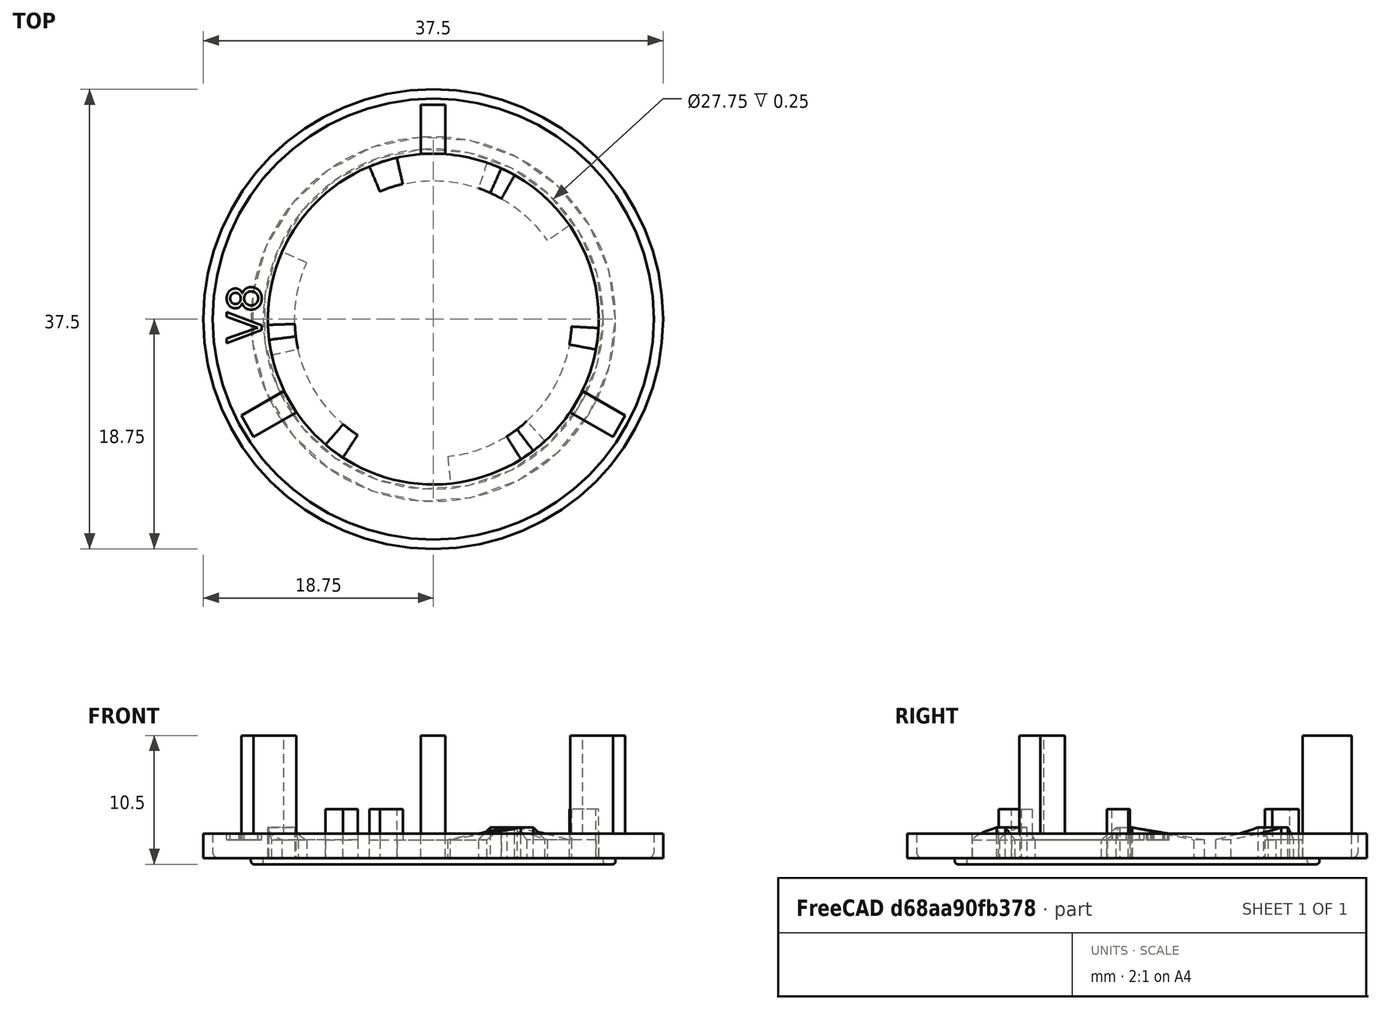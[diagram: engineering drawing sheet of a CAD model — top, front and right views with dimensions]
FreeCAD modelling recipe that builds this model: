
FCSTD DOCUMENT  (FreeCAD 0.19R21857 (Git))
Label: BayonetBaseFemaleV8
License: All rights reserved
LicenseURL: http://en.wikipedia.org/wiki/All_rights_reserved
objects: Sketcher::SketchObject×40, Part::Sweep×16, Part::MultiFuse×10, Part::Fillet×4, Part::Cylinder×3, Part::Mirroring×3, Part::Cut×2, PartDesign::Body×1, Part::Box×1, Image::ImagePlane×1, Part::FeaturePython×1, Part::Part2DObjectPython×1, Part::Extrusion×1, Mesh::Feature×1
note: 82 computed .brp shape members not serialized (recipe doc carries the construction recipe); baked Part::Feature solids carry a one-line shape summary decoded from their .brp

FEATURE [Part::Cylinder] Cylinder
  Angle = 360
  AttacherType = Attacher::AttachEngine3D
  Height = 2
  Radius = 18.75
FEATURE [Sketcher::SketchObject] Sketch  label="RampStart"
  Placement = pos=(0,0,0) rot=(1,0,0;1.5708rad)
  sketch-geometry (4):
    g0: LineSegment StartX=-13.5 StartY=0 StartZ=0 EndX=-13.5 EndY=1.5 EndZ=0
    g1: LineSegment StartX=-13.5 StartY=1.5 StartZ=0 EndX=-11.3 EndY=1.5 EndZ=0
    g2: LineSegment StartX=-11.3 StartY=1.5 StartZ=0 EndX=-11.3 EndY=0 EndZ=0
    g3: LineSegment StartX=-11.3 StartY=0 StartZ=0 EndX=-13.5 EndY=0 EndZ=0
  constraints (12):
    c: Coincident(g0,g1)
    c: Coincident(g1,g2)
    c: Coincident(g2,g3)
    c: Coincident(g3,g0)
    c: Parallel(g0,g2)
    c: Parallel(g1,g3)
    c: Horizontal(g3)
    c: Vertical(g2)
    c: DistanceY(g-1,g2) = 0
    c: DistanceX(g2,g-1) = 11.3
    c: DistanceX(g0,g-1) = 13.5
    c: DistanceY(g0,g0) = 1.5
FEATURE [Sketcher::SketchObject] Sketch001  label="InnerCircumference"
  Placement = pos=(0,0,0) rot=(1,0,0;3.14159rad)
  sketch-geometry (1):
    g0: Circle CenterX=0 CenterY=0 CenterZ=0 NormalX=0 NormalY=0 NormalZ=1 AngleXU=0 Radius=11
  constraints (1):
    c: Radius(g0) = 11
FEATURE [Sketcher::SketchObject] Sketch002  label="RampEnd"
  Placement = pos=(0,0,0) rot=(0.950615,-0.219467,-0.219467;1.62142rad)
  sketch-geometry (4):
    g0: LineSegment StartX=-13.5 StartY=0 StartZ=0 EndX=-13.5 EndY=2.5 EndZ=0
    g1: LineSegment StartX=-13.5 StartY=2.5 StartZ=0 EndX=-11.3 EndY=2.5 EndZ=0
    g2: LineSegment StartX=-11.3 StartY=2.5 StartZ=0 EndX=-11.3 EndY=0 EndZ=0
    g3: LineSegment StartX=-11.3 StartY=0 StartZ=0 EndX=-13.5 EndY=0 EndZ=0
  constraints (12):
    c: Coincident(g0,g1)
    c: Coincident(g1,g2)
    c: Coincident(g2,g3)
    c: Coincident(g3,g0)
    c: Parallel(g0,g2)
    c: Parallel(g1,g3)
    c: Horizontal(g3)
    c: Vertical(g2)
    c: DistanceY(g-1,g2) = 0
    c: DistanceX(g2,g-1) = 11.3
    c: DistanceX(g0,g-1) = 13.5
    c: DistanceY(g0,g0) = 2.5
FEATURE [Sketcher::SketchObject] Sketch003  label="RampFlat"
  Placement = pos=(0,0,0) rot=(0.930118,-0.259693,-0.259693;1.64318rad)
  sketch-geometry (4):
    g0: LineSegment StartX=-13.5 StartY=0 StartZ=0 EndX=-13.5 EndY=2.5 EndZ=0
    g1: LineSegment StartX=-13.5 StartY=2.5 StartZ=0 EndX=-11.3 EndY=2.5 EndZ=0
    g2: LineSegment StartX=-11.3 StartY=2.5 StartZ=0 EndX=-11.3 EndY=0 EndZ=0
    g3: LineSegment StartX=-11.3 StartY=0 StartZ=0 EndX=-13.5 EndY=0 EndZ=0
  constraints (12):
    c: Coincident(g0,g1)
    c: Coincident(g1,g2)
    c: Coincident(g2,g3)
    c: Coincident(g3,g0)
    c: Parallel(g0,g2)
    c: Parallel(g1,g3)
    c: Horizontal(g3)
    c: Vertical(g2)
    c: DistanceY(g-1,g2) = 0
    c: DistanceX(g2,g-1) = 11.3
    c: DistanceX(g0,g-1) = 13.5
    c: DistanceY(g0,g0) = 2.5
FEATURE [Sketcher::SketchObject] Sketch004  label="LockFlat"
  Placement = pos=(0,0,0) rot=(0.906297,-0.298852,-0.298852;1.66903rad)
  sketch-geometry (4):
    g0: LineSegment StartX=-13.5 StartY=0 StartZ=0 EndX=-13.5 EndY=1.5 EndZ=0
    g1: LineSegment StartX=-13.5 StartY=1.5 StartZ=0 EndX=-11.3 EndY=1.5 EndZ=0
    g2: LineSegment StartX=-11.3 StartY=1.5 StartZ=0 EndX=-11.3 EndY=0 EndZ=0
    g3: LineSegment StartX=-11.3 StartY=0 StartZ=0 EndX=-13.5 EndY=0 EndZ=0
  constraints (12):
    c: Coincident(g0,g1)
    c: Coincident(g1,g2)
    c: Coincident(g2,g3)
    c: Coincident(g3,g0)
    c: Parallel(g0,g2)
    c: Parallel(g1,g3)
    c: Horizontal(g3)
    c: Vertical(g2)
    c: DistanceY(g-1,g2) = 0
    c: DistanceX(g2,g-1) = 11.3
    c: DistanceX(g0,g-1) = 13.5
    c: DistanceY(g0,g0) = 1.5
FEATURE [Sketcher::SketchObject] Sketch005  label="LockFlatEnd"
  Placement = pos=(0,0,0) rot=(0.638387,-0.544271,-0.544271;2.00526rad)
  sketch-geometry (4):
    g0: LineSegment StartX=-13.5 StartY=0 StartZ=0 EndX=-13.5 EndY=1.5 EndZ=0
    g1: LineSegment StartX=-13.5 StartY=1.5 StartZ=0 EndX=-11.3 EndY=1.5 EndZ=0
    g2: LineSegment StartX=-11.3 StartY=1.5 StartZ=0 EndX=-11.3 EndY=0 EndZ=0
    g3: LineSegment StartX=-11.3 StartY=0 StartZ=0 EndX=-13.5 EndY=0 EndZ=0
  constraints (12):
    c: Coincident(g0,g1)
    c: Coincident(g1,g2)
    c: Coincident(g2,g3)
    c: Coincident(g3,g0)
    c: Parallel(g0,g2)
    c: Parallel(g1,g3)
    c: Horizontal(g3)
    c: Vertical(g2)
    c: DistanceY(g-1,g2) = 0
    c: DistanceX(g2,g-1) = 11.3
    c: DistanceX(g0,g-1) = 13.5
    c: DistanceY(g0,g0) = 1.5
FEATURE [Sketcher::SketchObject] Sketch006  label="RampPath"
  sketch-geometry (1):
    g0: ArcOfCircle CenterX=0 CenterY=0 CenterZ=0 NormalX=0 NormalY=0 NormalZ=1 AngleXU=0 Radius=11.0109 StartAngle=1.68589 EndAngle=3.14182
FEATURE [Sketcher::SketchObject] Sketch007  label="Path1"
  sketch-geometry (2):
    g0: ArcOfCircle CenterX=0 CenterY=0 CenterZ=0 NormalX=0 NormalY=0 NormalZ=1 AngleXU=0 Radius=11.3 StartAngle=2.68754 EndAngle=3.14132
    g1: GeomPoint X=-10.1564 Y=4.95359 Z=0
  constraints (3):
    c: Radius(g0) = 11.3
    c: Coincident(g-1,g0)
    c: Angle(g0) = 0.453786
FEATURE [PartDesign::Body] Body
  Group = -> [Sketch005,Sketch004,Sketch003,Sketch002,Sketch001,Sketch,Sketch006,Sketch007]
  Origin = -> Origin
FEATURE [Part::Sweep] Sweep
  Frenet = false
  Sections = -> [Sketch,Sketch002]
  Solid = true
  Spine = -> Sketch007 [Edge1]
  Transition = 1
FEATURE [Sketcher::SketchObject] Sketch008  label="Path2"
  sketch-geometry (1):
    g0: ArcOfCircle CenterX=0 CenterY=0 CenterZ=0 NormalX=0 NormalY=0 NormalZ=1 AngleXU=0 Radius=11.3 StartAngle=2.59707 EndAngle=2.68754
  constraints (2):
    c: Radius(g0) = 11.3
    c: Coincident(g0,g-1)
FEATURE [Sketcher::SketchObject] Sketch009  label="Path3"
  sketch-geometry (1):
    g0: ArcOfCircle CenterX=0 CenterY=0 CenterZ=0 NormalX=0 NormalY=0 NormalZ=1 AngleXU=0 Radius=11.3 StartAngle=2.50468 EndAngle=2.59704
  constraints (2):
    c: Radius(g0) = 11.3
    c: Coincident(g0,g-1)
FEATURE [Sketcher::SketchObject] Sketch010  label="Path4"
  sketch-geometry (1):
    g0: ArcOfCircle CenterX=0 CenterY=0 CenterZ=0 NormalX=0 NormalY=0 NormalZ=1 AngleXU=0 Radius=11.3 StartAngle=1.72935 EndAngle=2.50452
  constraints (2):
    c: Radius(g0) = 11.3
    c: Coincident(g0,g-1)
FEATURE [Part::Sweep] Sweep001
  Frenet = false
  Sections = -> [Sketch002,Sketch003]
  Solid = true
  Spine = -> Sketch008 [Edge1]
  Transition = 1
FEATURE [Part::Sweep] Sweep002
  Frenet = false
  Sections = -> [Sketch003,Sketch004]
  Solid = true
  Spine = -> Sketch009 [Edge1]
  Transition = 1
FEATURE [Part::Sweep] Sweep003
  Frenet = false
  Sections = -> [Sketch004,Sketch005]
  Solid = true
  Spine = -> Sketch010 [Edge1]
  Transition = 1
FEATURE [Part::MultiFuse] Fusion  label="Ramp"
  Shapes = -> [Sweep,Sweep001,Sweep002,Sweep003]
FEATURE [Sketcher::SketchObject] Sketch011  label="EndstopEnd"
  Placement = pos=(0,0,0) rot=(0.638387,-0.544271,-0.544271;2.00526rad)
  sketch-geometry (4):
    g0: LineSegment StartX=-13.5 StartY=0 StartZ=0 EndX=-13.5 EndY=4 EndZ=0
    g1: LineSegment StartX=-13.5 StartY=4 StartZ=0 EndX=-11.3 EndY=4 EndZ=0
    g2: LineSegment StartX=-11.3 StartY=4 StartZ=0 EndX=-11.3 EndY=0 EndZ=0
    g3: LineSegment StartX=-11.3 StartY=0 StartZ=0 EndX=-13.5 EndY=0 EndZ=0
  constraints (12):
    c: Coincident(g0,g1)
    c: Coincident(g1,g2)
    c: Coincident(g2,g3)
    c: Coincident(g3,g0)
    c: Parallel(g0,g2)
    c: Parallel(g1,g3)
    c: Horizontal(g3)
    c: Vertical(g2)
    c: DistanceY(g-1,g2) = 0
    c: DistanceX(g2,g-1) = 11.3
    c: DistanceX(g0,g-1) = 13.5
    c: DistanceY(g0,g0) = 4
FEATURE [Sketcher::SketchObject] Sketch012  label="EndstopStart"
  Placement = pos=(0,0,0) rot=(0.688237,-0.512996,-0.512996;1.93602rad)
  sketch-geometry (4):
    g0: LineSegment StartX=-13.5 StartY=0 StartZ=0 EndX=-13.5 EndY=4 EndZ=0
    g1: LineSegment StartX=-13.5 StartY=4 StartZ=0 EndX=-11.3 EndY=4 EndZ=0
    g2: LineSegment StartX=-11.3 StartY=4 StartZ=0 EndX=-11.3 EndY=0 EndZ=0
    g3: LineSegment StartX=-11.3 StartY=0 StartZ=0 EndX=-13.5 EndY=0 EndZ=0
  constraints (12):
    c: Coincident(g0,g1)
    c: Coincident(g1,g2)
    c: Coincident(g2,g3)
    c: Coincident(g3,g0)
    c: Parallel(g0,g2)
    c: Parallel(g1,g3)
    c: Horizontal(g3)
    c: Vertical(g2)
    c: DistanceY(g-1,g2) = 0
    c: DistanceX(g2,g-1) = 11.3
    c: DistanceX(g0,g-1) = 13.5
    c: DistanceY(g0,g0) = 4
FEATURE [Sketcher::SketchObject] Sketch013  label="EndstopPath"
  sketch-geometry (1):
    g0: ArcOfCircle CenterX=0 CenterY=0 CenterZ=0 NormalX=0 NormalY=0 NormalZ=1 AngleXU=0 Radius=11.3 StartAngle=1.72959 EndAngle=1.86043
  constraints (2):
    c: Radius(g0) = 11.3
    c: Coincident(g-1,g0)
FEATURE [Part::Sweep] Sweep004  label="EndStop"
  Frenet = false
  Sections = -> [Sketch012,Sketch011]
  Solid = true
  Spine = -> Sketch013 [Edge1]
  Transition = 1
FEATURE [Part::MultiFuse] Fusion001  label="RampWithEndstop"
  Shapes = -> [Fusion,Sweep004]
FEATURE [Part::Cylinder] Cylinder001
  Angle = 360
  AttacherType = Attacher::AttachEngine3D
  Height = 2
  Radius = 18
FEATURE [Part::Cylinder] Cylinder002
  Angle = 360
  AttacherType = Attacher::AttachEngine3D
  Height = 2
  Radius = 13.5
FEATURE [Part::Cut] Cut  label="Base"
  Base = -> Cylinder001
  Placement = pos=(0,0,2) rot=(1,0,0;3.14159rad)
  Tool = -> Cylinder002
FEATURE [Sketcher::SketchObject] Sketch015  label="GrooveProfile"
  Placement = pos=(0,0,0) rot=(1,0,0;1.5708rad)
  sketch-geometry (4):
    g0: LineSegment StartX=-14.875 StartY=-0.5 StartZ=0 EndX=-13.875 EndY=-0.5 EndZ=0
    g1: LineSegment StartX=-13.875 StartY=-0.5 StartZ=0 EndX=-13.875 EndY=0.5 EndZ=0
    g2: LineSegment StartX=-13.875 StartY=0.5 StartZ=0 EndX=-14.875 EndY=0.5 EndZ=0
    g3: LineSegment StartX=-14.875 StartY=0.5 StartZ=0 EndX=-14.875 EndY=-0.5 EndZ=0
  constraints (12):
    c: Coincident(g0,g1)
    c: Coincident(g1,g2)
    c: Coincident(g2,g3)
    c: Coincident(g3,g0)
    c: Horizontal(g0)
    c: Horizontal(g2)
    c: Vertical(g1)
    c: Vertical(g3)
    c: DistanceX(g0,g0) = 1
    c: Equal(g0,g1)
    c: DistanceY(g1,g-1) = -0.5
    c: DistanceX(g1,g-1) = 13.875
FEATURE [Sketcher::SketchObject] Sketch016  label="GroovePath"
  sketch-geometry (1):
    g0: Circle CenterX=0 CenterY=0 CenterZ=0 NormalX=0 NormalY=0 NormalZ=1 AngleXU=0 Radius=13.875
  constraints (2):
    c: Coincident(g0,g-1)
    c: Radius(g0) = 13.875
FEATURE [Part::Sweep] Sweep005  label="Groove"
  Frenet = false
  Sections = -> [Sketch015]
  Solid = true
  Spine = -> Sketch016 [Edge1]
  Transition = 1
FEATURE [Part::Box] Box  label="Cube"
  AttacherType = Attacher::AttachEngine3D
  Height = 10
  Length = 2
  Placement = pos=(-1,13.5,0) rot=(0,0,1;0rad)
  Width = 4
FEATURE [Part::Mirroring] Part__Mirroring  label="RampWithEndstopLong1"
  Base = (2.14696,3.57628e-07,2)
  Normal = (0,1,-1.19209e-07)
  Placement = pos=(0,0,0) rot=(0,0,-1;0.418879rad)
  Source = -> Fusion001
FEATURE [Sketcher::SketchObject] Sketch017  label="RampStart001"
  Placement = pos=(0,0,0) rot=(1,0,0;1.5708rad)
  sketch-geometry (4):
    g0: LineSegment StartX=-13.5 StartY=0 StartZ=0 EndX=-13.5 EndY=1.5 EndZ=0
    g1: LineSegment StartX=-13.5 StartY=1.5 StartZ=0 EndX=-11.3 EndY=1.5 EndZ=0
    g2: LineSegment StartX=-11.3 StartY=1.5 StartZ=0 EndX=-11.3 EndY=0 EndZ=0
    g3: LineSegment StartX=-11.3 StartY=0 StartZ=0 EndX=-13.5 EndY=0 EndZ=0
  constraints (12):
    c: Coincident(g0,g1)
    c: Coincident(g1,g2)
    c: Coincident(g2,g3)
    c: Coincident(g3,g0)
    c: Parallel(g0,g2)
    c: Parallel(g1,g3)
    c: Horizontal(g3)
    c: Vertical(g2)
    c: DistanceY(g-1,g2) = 0
    c: DistanceX(g2,g-1) = 11.3
    c: DistanceX(g0,g-1) = 13.5
    c: DistanceY(g0,g0) = 1.5
FEATURE [Sketcher::SketchObject] Sketch018  label="RampEnd001"
  Placement = pos=(0,0,0) rot=(0.950615,-0.219467,-0.219467;1.62142rad)
  sketch-geometry (4):
    g0: LineSegment StartX=-13.5 StartY=0 StartZ=0 EndX=-13.5 EndY=2.5 EndZ=0
    g1: LineSegment StartX=-13.5 StartY=2.5 StartZ=0 EndX=-11.3 EndY=2.5 EndZ=0
    g2: LineSegment StartX=-11.3 StartY=2.5 StartZ=0 EndX=-11.3 EndY=0 EndZ=0
    g3: LineSegment StartX=-11.3 StartY=0 StartZ=0 EndX=-13.5 EndY=0 EndZ=0
  constraints (12):
    c: Coincident(g0,g1)
    c: Coincident(g1,g2)
    c: Coincident(g2,g3)
    c: Coincident(g3,g0)
    c: Parallel(g0,g2)
    c: Parallel(g1,g3)
    c: Horizontal(g3)
    c: Vertical(g2)
    c: DistanceY(g-1,g2) = 0
    c: DistanceX(g2,g-1) = 11.3
    c: DistanceX(g0,g-1) = 13.5
    c: DistanceY(g0,g0) = 2.5
FEATURE [Sketcher::SketchObject] Sketch019  label="RampFlat001"
  Placement = pos=(0,0,0) rot=(0.930118,-0.259693,-0.259693;1.64318rad)
  sketch-geometry (4):
    g0: LineSegment StartX=-13.5 StartY=0 StartZ=0 EndX=-13.5 EndY=2.5 EndZ=0
    g1: LineSegment StartX=-13.5 StartY=2.5 StartZ=0 EndX=-11.3 EndY=2.5 EndZ=0
    g2: LineSegment StartX=-11.3 StartY=2.5 StartZ=0 EndX=-11.3 EndY=0 EndZ=0
    g3: LineSegment StartX=-11.3 StartY=0 StartZ=0 EndX=-13.5 EndY=0 EndZ=0
  constraints (12):
    c: Coincident(g0,g1)
    c: Coincident(g1,g2)
    c: Coincident(g2,g3)
    c: Coincident(g3,g0)
    c: Parallel(g0,g2)
    c: Parallel(g1,g3)
    c: Horizontal(g3)
    c: Vertical(g2)
    c: DistanceY(g-1,g2) = 0
    c: DistanceX(g2,g-1) = 11.3
    c: DistanceX(g0,g-1) = 13.5
    c: DistanceY(g0,g0) = 2.5
FEATURE [Sketcher::SketchObject] Sketch020  label="LockFlat001"
  Placement = pos=(0,0,0) rot=(0.906297,-0.298852,-0.298852;1.66903rad)
  sketch-geometry (4):
    g0: LineSegment StartX=-13.5 StartY=0 StartZ=0 EndX=-13.5 EndY=1.5 EndZ=0
    g1: LineSegment StartX=-13.5 StartY=1.5 StartZ=0 EndX=-11.3 EndY=1.5 EndZ=0
    g2: LineSegment StartX=-11.3 StartY=1.5 StartZ=0 EndX=-11.3 EndY=0 EndZ=0
    g3: LineSegment StartX=-11.3 StartY=0 StartZ=0 EndX=-13.5 EndY=0 EndZ=0
  constraints (12):
    c: Coincident(g0,g1)
    c: Coincident(g1,g2)
    c: Coincident(g2,g3)
    c: Coincident(g3,g0)
    c: Parallel(g0,g2)
    c: Parallel(g1,g3)
    c: Horizontal(g3)
    c: Vertical(g2)
    c: DistanceY(g-1,g2) = 0
    c: DistanceX(g2,g-1) = 11.3
    c: DistanceX(g0,g-1) = 13.5
    c: DistanceY(g0,g0) = 1.5
FEATURE [Sketcher::SketchObject] Sketch021  label="LockFlatEnd001"
  Placement = pos=(0,0,0) rot=(0.656406,-0.533447,-0.533447;1.97986rad)
  sketch-geometry (4):
    g0: LineSegment StartX=-13.5 StartY=0 StartZ=0 EndX=-13.5 EndY=1.5 EndZ=0
    g1: LineSegment StartX=-13.5 StartY=1.5 StartZ=0 EndX=-11.3 EndY=1.5 EndZ=0
    g2: LineSegment StartX=-11.3 StartY=1.5 StartZ=0 EndX=-11.3 EndY=0 EndZ=0
    g3: LineSegment StartX=-11.3 StartY=0 StartZ=0 EndX=-13.5 EndY=0 EndZ=0
  constraints (12):
    c: Coincident(g0,g1)
    c: Coincident(g1,g2)
    c: Coincident(g2,g3)
    c: Coincident(g3,g0)
    c: Parallel(g0,g2)
    c: Parallel(g1,g3)
    c: Horizontal(g3)
    c: Vertical(g2)
    c: DistanceY(g-1,g2) = 0
    c: DistanceX(g2,g-1) = 11.3
    c: DistanceX(g0,g-1) = 13.5
    c: DistanceY(g0,g0) = 1.5
FEATURE [Sketcher::SketchObject] Sketch022  label="Path005"
  sketch-geometry (2):
    g0: ArcOfCircle CenterX=0 CenterY=0 CenterZ=0 NormalX=0 NormalY=0 NormalZ=1 AngleXU=0 Radius=11.3 StartAngle=2.68754 EndAngle=3.14132
    g1: GeomPoint X=-10.1564 Y=4.95359 Z=0
  constraints (3):
    c: Radius(g0) = 11.3
    c: Coincident(g-1,g0)
    c: Angle(g0) = 0.453786
FEATURE [Sketcher::SketchObject] Sketch023  label="Path006"
  sketch-geometry (1):
    g0: ArcOfCircle CenterX=0 CenterY=0 CenterZ=0 NormalX=0 NormalY=0 NormalZ=1 AngleXU=0 Radius=11.3 StartAngle=2.59707 EndAngle=2.68754
  constraints (2):
    c: Radius(g0) = 11.3
    c: Coincident(g0,g-1)
FEATURE [Sketcher::SketchObject] Sketch024  label="Path007"
  sketch-geometry (1):
    g0: ArcOfCircle CenterX=0 CenterY=0 CenterZ=0 NormalX=0 NormalY=0 NormalZ=1 AngleXU=0 Radius=11.3 StartAngle=2.50468 EndAngle=2.59704
  constraints (2):
    c: Radius(g0) = 11.3
    c: Coincident(g0,g-1)
FEATURE [Sketcher::SketchObject] Sketch025  label="Path008"
  sketch-geometry (1):
    g0: ArcOfCircle CenterX=0 CenterY=0 CenterZ=0 NormalX=0 NormalY=0 NormalZ=1 AngleXU=0 Radius=11.3 StartAngle=1.77654 EndAngle=2.50452
  constraints (2):
    c: Radius(g0) = 11.3
    c: Coincident(g0,g-1)
FEATURE [Part::Sweep] Sweep006
  Frenet = false
  Sections = -> [Sketch018,Sketch019]
  Solid = true
  Spine = -> Sketch023 [Edge1]
  Transition = 1
FEATURE [Part::Sweep] Sweep007
  Frenet = false
  Sections = -> [Sketch019,Sketch020]
  Solid = true
  Spine = -> Sketch024 [Edge1]
  Transition = 1
FEATURE [Part::Sweep] Sweep008
  Frenet = false
  Sections = -> [Sketch020,Sketch021]
  Solid = true
  Spine = -> Sketch025 [Edge1]
  Transition = 1
FEATURE [Sketcher::SketchObject] Sketch026  label="EndstopEnd001"
  Placement = pos=(0,0,0) rot=(0.656406,-0.533447,-0.533447;1.97986rad)
  sketch-geometry (4):
    g0: LineSegment StartX=-13.5 StartY=0 StartZ=0 EndX=-13.5 EndY=4 EndZ=0
    g1: LineSegment StartX=-13.5 StartY=4 StartZ=0 EndX=-11.3 EndY=4 EndZ=0
    g2: LineSegment StartX=-11.3 StartY=4 StartZ=0 EndX=-11.3 EndY=0 EndZ=0
    g3: LineSegment StartX=-11.3 StartY=0 StartZ=0 EndX=-13.5 EndY=0 EndZ=0
  constraints (12):
    c: Coincident(g0,g1)
    c: Coincident(g1,g2)
    c: Coincident(g2,g3)
    c: Coincident(g3,g0)
    c: Parallel(g0,g2)
    c: Parallel(g1,g3)
    c: Horizontal(g3)
    c: Vertical(g2)
    c: DistanceY(g-1,g2) = 0
    c: DistanceX(g2,g-1) = 11.3
    c: DistanceX(g0,g-1) = 13.5
    c: DistanceY(g0,g0) = 4
FEATURE [Sketcher::SketchObject] Sketch027  label="EndstopStart001"
  Placement = pos=(0,0,0) rot=(0.722291,-0.489028,-0.489028;1.89053rad)
  sketch-geometry (4):
    g0: LineSegment StartX=-13.5 StartY=0 StartZ=0 EndX=-13.5 EndY=4 EndZ=0
    g1: LineSegment StartX=-13.5 StartY=4 StartZ=0 EndX=-11.3 EndY=4 EndZ=0
    g2: LineSegment StartX=-11.3 StartY=4 StartZ=0 EndX=-11.3 EndY=0 EndZ=0
    g3: LineSegment StartX=-11.3 StartY=0 StartZ=0 EndX=-13.5 EndY=0 EndZ=0
  constraints (12):
    c: Coincident(g0,g1)
    c: Coincident(g1,g2)
    c: Coincident(g2,g3)
    c: Coincident(g3,g0)
    c: Parallel(g0,g2)
    c: Parallel(g1,g3)
    c: Horizontal(g3)
    c: Vertical(g2)
    c: DistanceY(g-1,g2) = 0
    c: DistanceX(g2,g-1) = 11.3
    c: DistanceX(g0,g-1) = 13.5
    c: DistanceY(g0,g0) = 4
FEATURE [Sketcher::SketchObject] Sketch028  label="EndstopPath001"
  sketch-geometry (1):
    g0: ArcOfCircle CenterX=0 CenterY=0 CenterZ=0 NormalX=0 NormalY=0 NormalZ=1 AngleXU=0 Radius=11.3 StartAngle=1.77684 EndAngle=1.95126
  constraints (2):
    c: Radius(g0) = 11.3
    c: Coincident(g-1,g0)
FEATURE [Part::Sweep] Sweep009  label="EndStop001"
  Frenet = false
  Sections = -> [Sketch027,Sketch026]
  Solid = true
  Spine = -> Sketch028 [Edge1]
  Transition = 1
FEATURE [Part::Sweep] Sweep010
  Frenet = false
  Sections = -> [Sketch017,Sketch018]
  Solid = true
  Spine = -> Sketch022 [Edge1]
  Transition = 1
FEATURE [Part::MultiFuse] Fusion003  label="Ramp001"
  Shapes = -> [Sweep010,Sweep006,Sweep007,Sweep008]
FEATURE [Part::MultiFuse] Fusion002  label="RampWithEndstopShort"
  Placement = pos=(0,0,0) rot=(0,0,1;0.139626rad)
  Shapes = -> [Fusion003,Sweep009]
FEATURE [Part::Mirroring] Part__Mirroring001  label="RampWithEndstopShort 1"
  Base = (-7.97635,3.57628e-07,2)
  Normal = (0,1,-1.19209e-07)
  Placement = pos=(0,0,0) rot=(0,0,1;3.88336rad)
  Source = -> Fusion002
FEATURE [Part::Fillet] Fillet001
  Base = -> Sweep005
  Edges = 1 edges r=0.25: [Edge1]
FEATURE [Part::Fillet] Fillet002
  Base = -> Fillet001
  Edges = 1 edges r=0.25: [Edge3]
FEATURE [Image::ImagePlane] ImagePlane
  Placement = pos=(1,5.5,3) rot=(0,1,0;3.14159rad)
  XSize = 50.2916
  YSize = 59.2323
FEATURE [Part::Fillet] Fillet
  Base = -> Cut
  Edges = 1 edges r=0.5: [Edge1]
FEATURE [Sketcher::SketchObject] Sketch029  label="RampStart002"
  Placement = pos=(0,0,0) rot=(1,0,0;1.5708rad)
  sketch-geometry (4):
    g0: LineSegment StartX=-13.5 StartY=0 StartZ=0 EndX=-13.5 EndY=1.5 EndZ=0
    g1: LineSegment StartX=-13.5 StartY=1.5 StartZ=0 EndX=-11.3 EndY=1.5 EndZ=0
    g2: LineSegment StartX=-11.3 StartY=1.5 StartZ=0 EndX=-11.3 EndY=0 EndZ=0
    g3: LineSegment StartX=-11.3 StartY=0 StartZ=0 EndX=-13.5 EndY=0 EndZ=0
  constraints (12):
    c: Coincident(g0,g1)
    c: Coincident(g1,g2)
    c: Coincident(g2,g3)
    c: Coincident(g3,g0)
    c: Parallel(g0,g2)
    c: Parallel(g1,g3)
    c: Horizontal(g3)
    c: Vertical(g2)
    c: DistanceY(g-1,g2) = 0
    c: DistanceX(g2,g-1) = 11.3
    c: DistanceX(g0,g-1) = 13.5
    c: DistanceY(g0,g0) = 1.5
FEATURE [Sketcher::SketchObject] Sketch030  label="RampEnd002"
  Placement = pos=(0,0,0) rot=(0.950615,-0.219467,-0.219467;1.62142rad)
  sketch-geometry (4):
    g0: LineSegment StartX=-13.5 StartY=0 StartZ=0 EndX=-13.5 EndY=2.5 EndZ=0
    g1: LineSegment StartX=-13.5 StartY=2.5 StartZ=0 EndX=-11.3 EndY=2.5 EndZ=0
    g2: LineSegment StartX=-11.3 StartY=2.5 StartZ=0 EndX=-11.3 EndY=0 EndZ=0
    g3: LineSegment StartX=-11.3 StartY=0 StartZ=0 EndX=-13.5 EndY=0 EndZ=0
  constraints (12):
    c: Coincident(g0,g1)
    c: Coincident(g1,g2)
    c: Coincident(g2,g3)
    c: Coincident(g3,g0)
    c: Parallel(g0,g2)
    c: Parallel(g1,g3)
    c: Horizontal(g3)
    c: Vertical(g2)
    c: DistanceY(g-1,g2) = 0
    c: DistanceX(g2,g-1) = 11.3
    c: DistanceX(g0,g-1) = 13.5
    c: DistanceY(g0,g0) = 2.5
FEATURE [Sketcher::SketchObject] Sketch031  label="RampFlat002"
  Placement = pos=(0,0,0) rot=(0.930118,-0.259693,-0.259693;1.64318rad)
  sketch-geometry (4):
    g0: LineSegment StartX=-13.5 StartY=0 StartZ=0 EndX=-13.5 EndY=2.5 EndZ=0
    g1: LineSegment StartX=-13.5 StartY=2.5 StartZ=0 EndX=-11.3 EndY=2.5 EndZ=0
    g2: LineSegment StartX=-11.3 StartY=2.5 StartZ=0 EndX=-11.3 EndY=0 EndZ=0
    g3: LineSegment StartX=-11.3 StartY=0 StartZ=0 EndX=-13.5 EndY=0 EndZ=0
  constraints (12):
    c: Coincident(g0,g1)
    c: Coincident(g1,g2)
    c: Coincident(g2,g3)
    c: Coincident(g3,g0)
    c: Parallel(g0,g2)
    c: Parallel(g1,g3)
    c: Horizontal(g3)
    c: Vertical(g2)
    c: DistanceY(g-1,g2) = 0
    c: DistanceX(g2,g-1) = 11.3
    c: DistanceX(g0,g-1) = 13.5
    c: DistanceY(g0,g0) = 2.5
FEATURE [Sketcher::SketchObject] Sketch032  label="LockFlat002"
  Placement = pos=(0,0,0) rot=(0.906297,-0.298852,-0.298852;1.66903rad)
  sketch-geometry (4):
    g0: LineSegment StartX=-13.5 StartY=0 StartZ=0 EndX=-13.5 EndY=1.5 EndZ=0
    g1: LineSegment StartX=-13.5 StartY=1.5 StartZ=0 EndX=-11.3 EndY=1.5 EndZ=0
    g2: LineSegment StartX=-11.3 StartY=1.5 StartZ=0 EndX=-11.3 EndY=0 EndZ=0
    g3: LineSegment StartX=-11.3 StartY=0 StartZ=0 EndX=-13.5 EndY=0 EndZ=0
  constraints (12):
    c: Coincident(g0,g1)
    c: Coincident(g1,g2)
    c: Coincident(g2,g3)
    c: Coincident(g3,g0)
    c: Parallel(g0,g2)
    c: Parallel(g1,g3)
    c: Horizontal(g3)
    c: Vertical(g2)
    c: DistanceY(g-1,g2) = 0
    c: DistanceX(g2,g-1) = 11.3
    c: DistanceX(g0,g-1) = 13.5
    c: DistanceY(g0,g0) = 1.5
FEATURE [Sketcher::SketchObject] Sketch033  label="LockFlatEnd002"
  Placement = pos=(0,0,0) rot=(0.638387,-0.544271,-0.544271;2.00526rad)
  sketch-geometry (4):
    g0: LineSegment StartX=-13.5 StartY=0 StartZ=0 EndX=-13.5 EndY=1.5 EndZ=0
    g1: LineSegment StartX=-13.5 StartY=1.5 StartZ=0 EndX=-11.3 EndY=1.5 EndZ=0
    g2: LineSegment StartX=-11.3 StartY=1.5 StartZ=0 EndX=-11.3 EndY=0 EndZ=0
    g3: LineSegment StartX=-11.3 StartY=0 StartZ=0 EndX=-13.5 EndY=0 EndZ=0
  constraints (12):
    c: Coincident(g0,g1)
    c: Coincident(g1,g2)
    c: Coincident(g2,g3)
    c: Coincident(g3,g0)
    c: Parallel(g0,g2)
    c: Parallel(g1,g3)
    c: Horizontal(g3)
    c: Vertical(g2)
    c: DistanceY(g-1,g2) = 0
    c: DistanceX(g2,g-1) = 11.3
    c: DistanceX(g0,g-1) = 13.5
    c: DistanceY(g0,g0) = 1.5
FEATURE [Sketcher::SketchObject] Sketch034  label="Path009"
  sketch-geometry (2):
    g0: ArcOfCircle CenterX=0 CenterY=0 CenterZ=0 NormalX=0 NormalY=0 NormalZ=1 AngleXU=0 Radius=11.3 StartAngle=2.68754 EndAngle=3.14132
    g1: GeomPoint X=-10.1564 Y=4.95359 Z=0
  constraints (3):
    c: Radius(g0) = 11.3
    c: Coincident(g-1,g0)
    c: Angle(g0) = 0.453786
FEATURE [Part::Sweep] Sweep011
  Frenet = false
  Sections = -> [Sketch029,Sketch030]
  Solid = true
  Spine = -> Sketch034 [Edge1]
  Transition = 1
FEATURE [Sketcher::SketchObject] Sketch035  label="Path010"
  sketch-geometry (1):
    g0: ArcOfCircle CenterX=0 CenterY=0 CenterZ=0 NormalX=0 NormalY=0 NormalZ=1 AngleXU=0 Radius=11.3 StartAngle=2.59707 EndAngle=2.68754
  constraints (2):
    c: Radius(g0) = 11.3
    c: Coincident(g0,g-1)
FEATURE [Sketcher::SketchObject] Sketch036  label="Path011"
  sketch-geometry (1):
    g0: ArcOfCircle CenterX=0 CenterY=0 CenterZ=0 NormalX=0 NormalY=0 NormalZ=1 AngleXU=0 Radius=11.3 StartAngle=2.50468 EndAngle=2.59704
  constraints (2):
    c: Radius(g0) = 11.3
    c: Coincident(g0,g-1)
FEATURE [Sketcher::SketchObject] Sketch037  label="Path012"
  sketch-geometry (1):
    g0: ArcOfCircle CenterX=0 CenterY=0 CenterZ=0 NormalX=0 NormalY=0 NormalZ=1 AngleXU=0 Radius=11.3 StartAngle=1.72961 EndAngle=2.50452
  constraints (2):
    c: Radius(g0) = 11.3
    c: Coincident(g0,g-1)
FEATURE [Part::Sweep] Sweep012
  Frenet = false
  Sections = -> [Sketch030,Sketch031]
  Solid = true
  Spine = -> Sketch035 [Edge1]
  Transition = 1
FEATURE [Part::Sweep] Sweep013
  Frenet = false
  Sections = -> [Sketch031,Sketch032]
  Solid = true
  Spine = -> Sketch036 [Edge1]
  Transition = 1
FEATURE [Part::Sweep] Sweep014
  Frenet = false
  Sections = -> [Sketch032,Sketch033]
  Solid = true
  Spine = -> Sketch037 [Edge1]
  Transition = 1
FEATURE [Part::MultiFuse] Fusion004  label="Ramp002"
  Shapes = -> [Sweep011,Sweep012,Sweep013,Sweep014]
FEATURE [Sketcher::SketchObject] Sketch038  label="EndstopEnd002"
  Placement = pos=(0,0,0) rot=(0.638387,-0.544271,-0.544271;2.00526rad)
  sketch-geometry (4):
    g0: LineSegment StartX=-13.5 StartY=0 StartZ=0 EndX=-13.5 EndY=4 EndZ=0
    g1: LineSegment StartX=-13.5 StartY=4 StartZ=0 EndX=-11.3 EndY=4 EndZ=0
    g2: LineSegment StartX=-11.3 StartY=4 StartZ=0 EndX=-11.3 EndY=0 EndZ=0
    g3: LineSegment StartX=-11.3 StartY=0 StartZ=0 EndX=-13.5 EndY=0 EndZ=0
  constraints (12):
    c: Coincident(g0,g1)
    c: Coincident(g1,g2)
    c: Coincident(g2,g3)
    c: Coincident(g3,g0)
    c: Parallel(g0,g2)
    c: Parallel(g1,g3)
    c: Horizontal(g3)
    c: Vertical(g2)
    c: DistanceY(g-1,g2) = 0
    c: DistanceX(g2,g-1) = 11.3
    c: DistanceX(g0,g-1) = 13.5
    c: DistanceY(g0,g0) = 4
FEATURE [Sketcher::SketchObject] Sketch039  label="EndstopStart002"
  Placement = pos=(0,0,0) rot=(0.688237,-0.512996,-0.512996;1.93602rad)
  sketch-geometry (4):
    g0: LineSegment StartX=-13.5 StartY=0 StartZ=0 EndX=-13.5 EndY=4 EndZ=0
    g1: LineSegment StartX=-13.5 StartY=4 StartZ=0 EndX=-11.3 EndY=4 EndZ=0
    g2: LineSegment StartX=-11.3 StartY=4 StartZ=0 EndX=-11.3 EndY=0 EndZ=0
    g3: LineSegment StartX=-11.3 StartY=0 StartZ=0 EndX=-13.5 EndY=0 EndZ=0
  constraints (12):
    c: Coincident(g0,g1)
    c: Coincident(g1,g2)
    c: Coincident(g2,g3)
    c: Coincident(g3,g0)
    c: Parallel(g0,g2)
    c: Parallel(g1,g3)
    c: Horizontal(g3)
    c: Vertical(g2)
    c: DistanceY(g-1,g2) = 0
    c: DistanceX(g2,g-1) = 11.3
    c: DistanceX(g0,g-1) = 13.5
    c: DistanceY(g0,g0) = 4
FEATURE [Sketcher::SketchObject] Sketch040  label="EndstopPath002"
  sketch-geometry (1):
    g0: ArcOfCircle CenterX=0 CenterY=0 CenterZ=0 NormalX=0 NormalY=0 NormalZ=1 AngleXU=0 Radius=11.3 StartAngle=1.72959 EndAngle=1.86043
  constraints (2):
    c: Radius(g0) = 11.3
    c: Coincident(g-1,g0)
FEATURE [Part::Sweep] Sweep015  label="EndStop002"
  Frenet = false
  Sections = -> [Sketch039,Sketch038]
  Solid = true
  Spine = -> Sketch040 [Edge1]
  Transition = 1
FEATURE [Part::MultiFuse] Fusion005  label="RampWithEndstop001"
  Shapes = -> [Fusion004,Sweep015]
FEATURE [Part::Mirroring] Part__Mirroring002  label="RampWithEndstopLong2"
  Base = (2.14696,3.57628e-07,2)
  Normal = (0,1,-1.19209e-07)
  Placement = pos=(0,0,0) rot=(0,0,1;1.67552rad)
  Source = -> Fusion005
FEATURE [Part::MultiFuse] Fusion006  label="Ramps"
  Shapes = -> [Part__Mirroring002,Part__Mirroring001,Part__Mirroring]
FEATURE [Part::Fillet] Fillet003
  Base = -> Cut
  Edges = 1 edges r=0.5: [Edge1]
FEATURE [Part::MultiFuse] Fusion007  label="Base001"
  Shapes = -> [Fillet,Fillet002,Fillet003]
FEATURE [Part::FeaturePython] Array  label="testhandles"  # Draft array (typed FeaturePython)
  Angle = 360
  ArrayType = 1
  Axis = (0,0,1)
  Base = -> Box
  Center = (0,0,0)
  Count = 3
  ExpandArray = false
  Fuse = false
  IntervalAxis = (0,0,0)
  IntervalX = (105,0,0)
  IntervalY = (0,100,0)
  IntervalZ = (0,0,100)
  NumberCircles = 3
  NumberPolar = 3
  NumberX = 2
  NumberY = 2
  NumberZ = 1
  PlacementList = 3 placements: [(-1,13.5,0),(-11.1913,-7.61603,0),(12.1913,-5.88397,0)]
  RadialDistance = 50
  ScaleList = (3) [(1,1,1),(1,1,1),(1,1,1)]
  Symmetry = 1
  TangentialDistance = 25
FEATURE [Part::Part2DObjectPython] ShapeString  # Draft 2D object (typed FeaturePython)
  FontFile = <path>
  Size = 3
  String = V8
  Tracking = 0
FEATURE [Part::Extrusion] Extrude
  Base = -> ShapeString
  Dir = (0,0,1)
  DirMode = 2
  FaceMakerClass = Part::FaceMakerBullseye
  LengthFwd = 0.5
  LengthRev = 0
  Placement = pos=(-14,-2,1.5) rot=(0,0,1;1.5708rad)
  Solid = false
  Symmetric = false
FEATURE [Part::Cut] Cut001
  Base = -> Fusion007
  Tool = -> Extrude
FEATURE [Mesh::Feature] BayonetMtestV2
  Placement = pos=(0,0,-1.8) rot=(0,0,1;1.02102rad)
FEATURE [Part::MultiFuse] Fusion008
  Shapes = -> [Cut001,Fusion006]
FEATURE [Part::MultiFuse] Fusion009  label="BayonetFtestV8"
  Shapes = -> [Fusion008,Array]
note: 1 file-system path scrubbed to <path> (originals preserved in the JSON sidecar)
